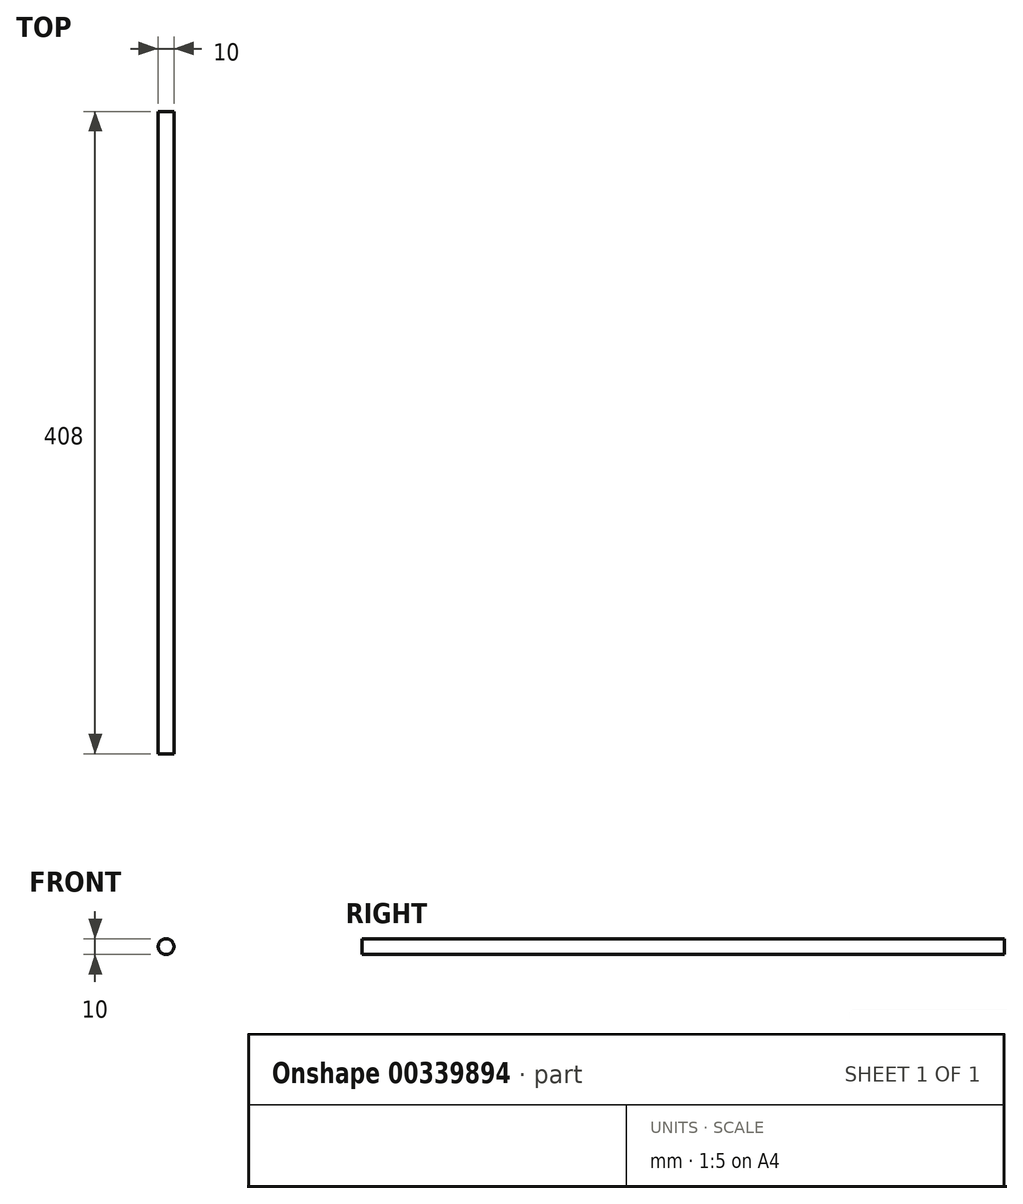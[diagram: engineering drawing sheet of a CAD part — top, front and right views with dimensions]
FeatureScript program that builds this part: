
annotation { "Feature Type Name" : "Feature", "Feature Type Description" : "" }
export const myFeature = defineFeature(function(context is Context, id is Id, definition is map)
    precondition{}
    {
        {
            var Q0;
            Q0=qCreatedBy(makeId("Front.planeOp"),FACE);
            var sketch = newSketch(context, id + "F0", { "sketchPlane" : qUnion([Q0])});
            skCircle(sketch, "E0", {"center": v(-10.52, 19.23) * mm, "radius": 5 * mm});
            skSolve(sketch);
        }
        {
            var Q0;
            Q0 = qConstructionFilter(qBodyType(qCreatedBy(id + "F0" ,EDGE), BodyType.WIRE), ConstructionObject.NO);
            extrude(context, id + "F1", {"bodyType" : ExtendedToolBodyType.SURFACE, "surfaceEntities" : qUnion([Q0]), "offsetDistance" : 25 * mm, "depth" : 408 * mm});
        }
    });
